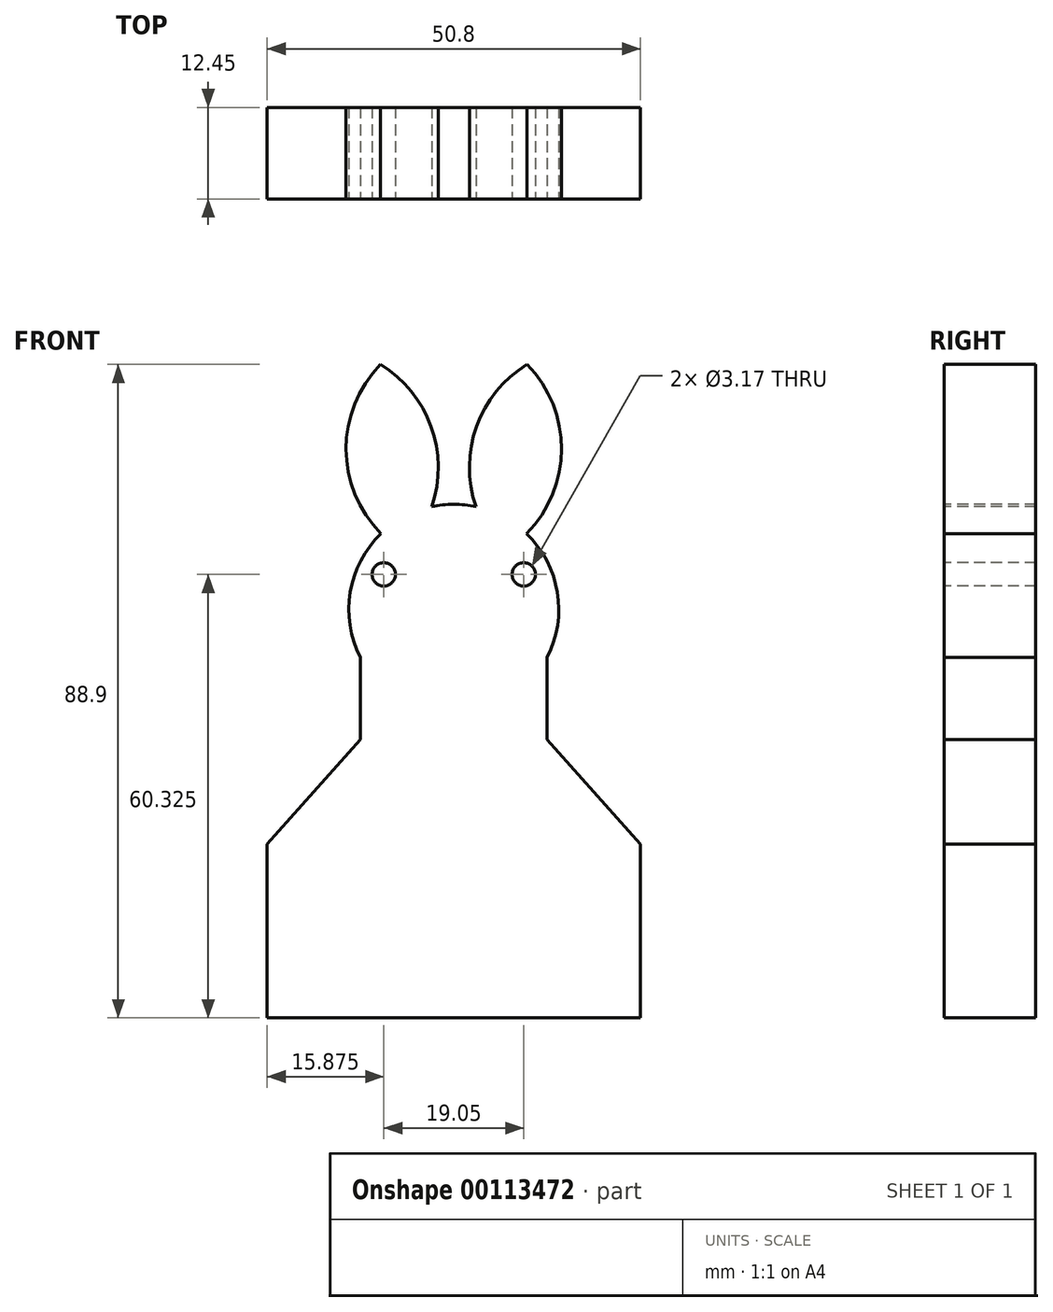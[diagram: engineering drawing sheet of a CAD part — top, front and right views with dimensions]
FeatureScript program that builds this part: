
annotation { "Feature Type Name" : "Feature", "Feature Type Description" : "" }
export const myFeature = defineFeature(function(context is Context, id is Id, definition is map)
    precondition{}
    {
        {
            var Q0;
            Q0=qCreatedBy(makeId("Front.planeOp"),FACE);
            var sketch = newSketch(context, id + "F0", { "sketchPlane" : qUnion([Q0])});
            skLineSegment(sketch, "E0", {"start": v(0, 0) * mm, "end": v(0, 88.9) * mm, "construction": true});
            skCircle(sketch, "E1", {"center": v(0, 55.56) * mm, "radius": 14.29 * mm});
            skLineSegment(sketch, "E2", {"start": v(-12.7, 37.85) * mm, "end": v(-12.7, 49.02) * mm});
            skLineSegment(sketch, "E3", {"start": v(-12.7, 37.85) * mm, "end": v(-25.4, 23.64) * mm});
            skLineSegment(sketch, "E4", {"start": v(-25.4, 23.64) * mm, "end": v(-25.4, 0) * mm});
            skLineSegment(sketch, "E5", {"start": v(-25.4, 0) * mm, "end": v(0, 0) * mm});
            skLineSegment(sketch, "E6.MirrorCS", {"start": v(25.4, 0) * mm, "end": v(0, 0) * mm});
            skLineSegment(sketch, "E7.MirrorCS", {"start": v(25.4, 23.64) * mm, "end": v(25.4, 0) * mm});
            skLineSegment(sketch, "E8.MirrorCS", {"start": v(12.7, 37.85) * mm, "end": v(12.7, 49.02) * mm});
            skLineSegment(sketch, "E9.MirrorCS", {"start": v(12.7, 37.85) * mm, "end": v(25.4, 23.64) * mm});
            skArc(sketch, "E10", {"start": v(-9.98, 88.9) * mm, "mid": v(-14.65, 77.36) * mm, "end": v(-9.9, 65.86) * mm});
            skArc(sketch, "E11", {"start": v(-3.02, 69.53) * mm, "mid": v(-3.1, 80.44) * mm, "end": v(-9.98, 88.9) * mm});
            skArc(sketch, "E12.MirrorCS", {"start": v(9.98, 88.9) * mm, "mid": v(14.65, 77.36) * mm, "end": v(9.9, 65.86) * mm});
            skArc(sketch, "E13.MirrorCS", {"start": v(3.02, 69.53) * mm, "mid": v(3.1, 80.44) * mm, "end": v(9.98, 88.9) * mm});
            skCircle(sketch, "E14", {"center": v(-9.53, 60.33) * mm, "radius": 1.59 * mm});
            skCircle(sketch, "E15.MirrorC", {"center": v(9.53, 60.33) * mm, "radius": 1.59 * mm});
            skSolve(sketch);
        }
        {
            var Q0;
            Q0 = qSketchRegion(id + "F0", true);
            extrude(context, id + "F1", {"entities" : qUnion([Q0]), "oppositeDirection" : true, "depth" : 12.45 * mm});
        }
    });
